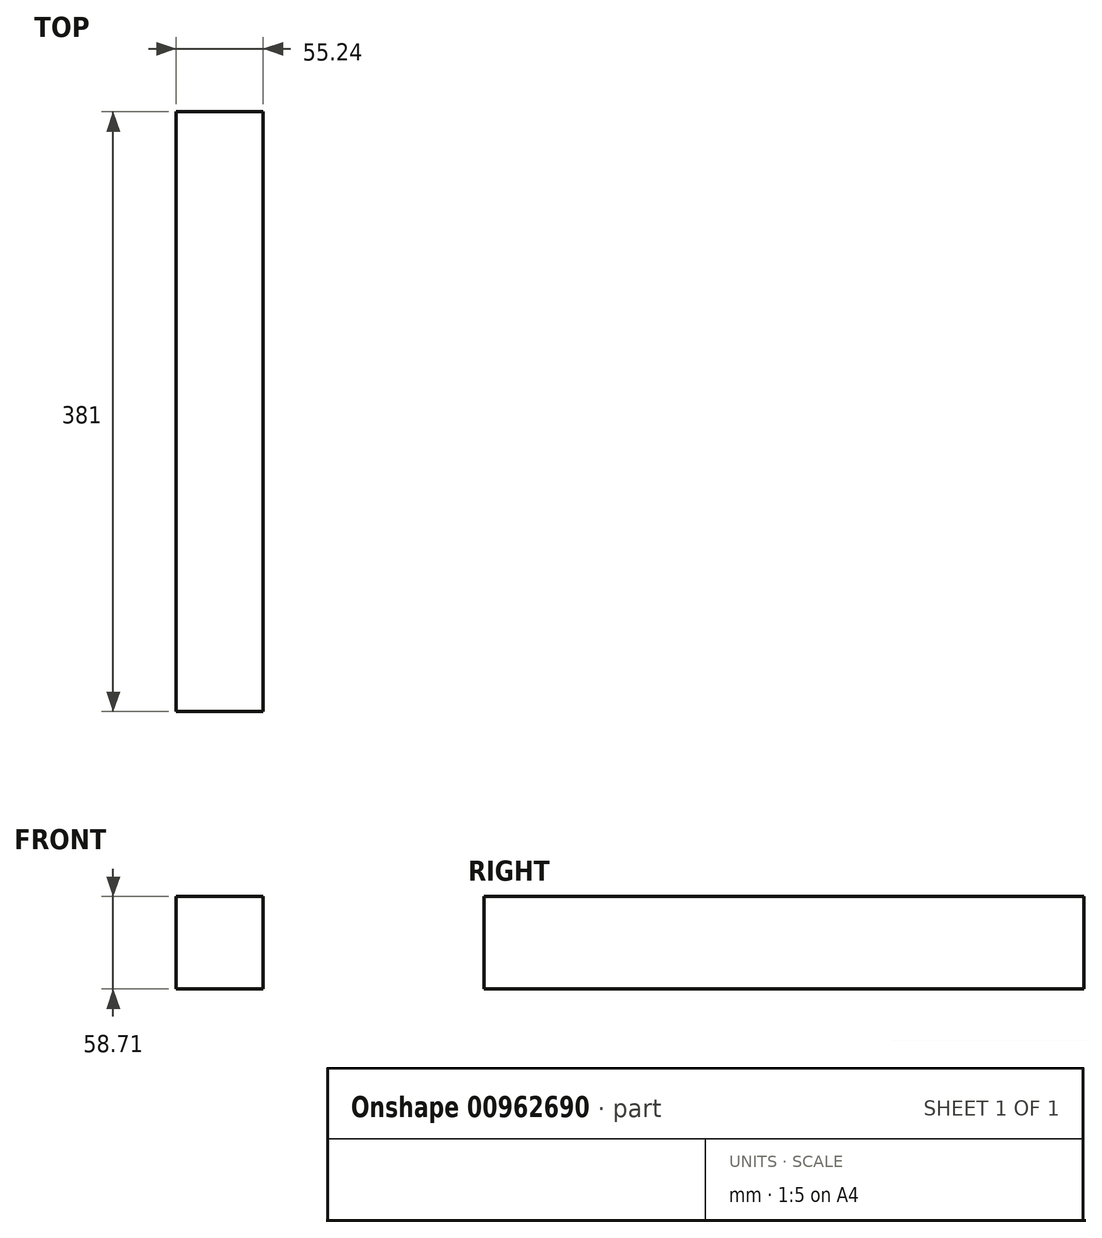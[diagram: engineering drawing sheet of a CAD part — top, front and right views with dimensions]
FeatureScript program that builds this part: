
annotation { "Feature Type Name" : "Feature", "Feature Type Description" : "" }
export const myFeature = defineFeature(function(context is Context, id is Id, definition is map)
    precondition{}
    {
        {
            var Q0;
            Q0=qCreatedBy(makeId("Front.planeOp"),FACE);
            var sketch = newSketch(context, id + "F0", { "sketchPlane" : qUnion([Q0])});
            skLineSegment(sketch, "E0.bottom", {"start": v(0, 0) * mm, "end": v(55.24, 0) * mm});
            skLineSegment(sketch, "E0.top", {"start": v(0, 58.7) * mm, "end": v(55.24, 58.7) * mm});
            skLineSegment(sketch, "E0.left", {"start": v(0, 0) * mm, "end": v(0, 58.7) * mm});
            skLineSegment(sketch, "E0.right", {"start": v(55.24, 0) * mm, "end": v(55.24, 58.7) * mm});
            skSolve(sketch);
        }
        {
            var Q0;
            Q0=makeQuery(id+"F0.imprint","IMPRINT",FACE,{"disambiguationData":[TD([[makeQuery(id+"F0.imprint","IMPRINT",EDGE,{"derivedFrom":sQuery(id+"F0.wireOp",EDGE,"E0.bottom")}),1.0]])]});
            extrude(context, id + "F1", {"entities" : qUnion([Q0]), "depth" : 381 * mm, "offsetDistance" : 25.4 * mm});
        }
    });
